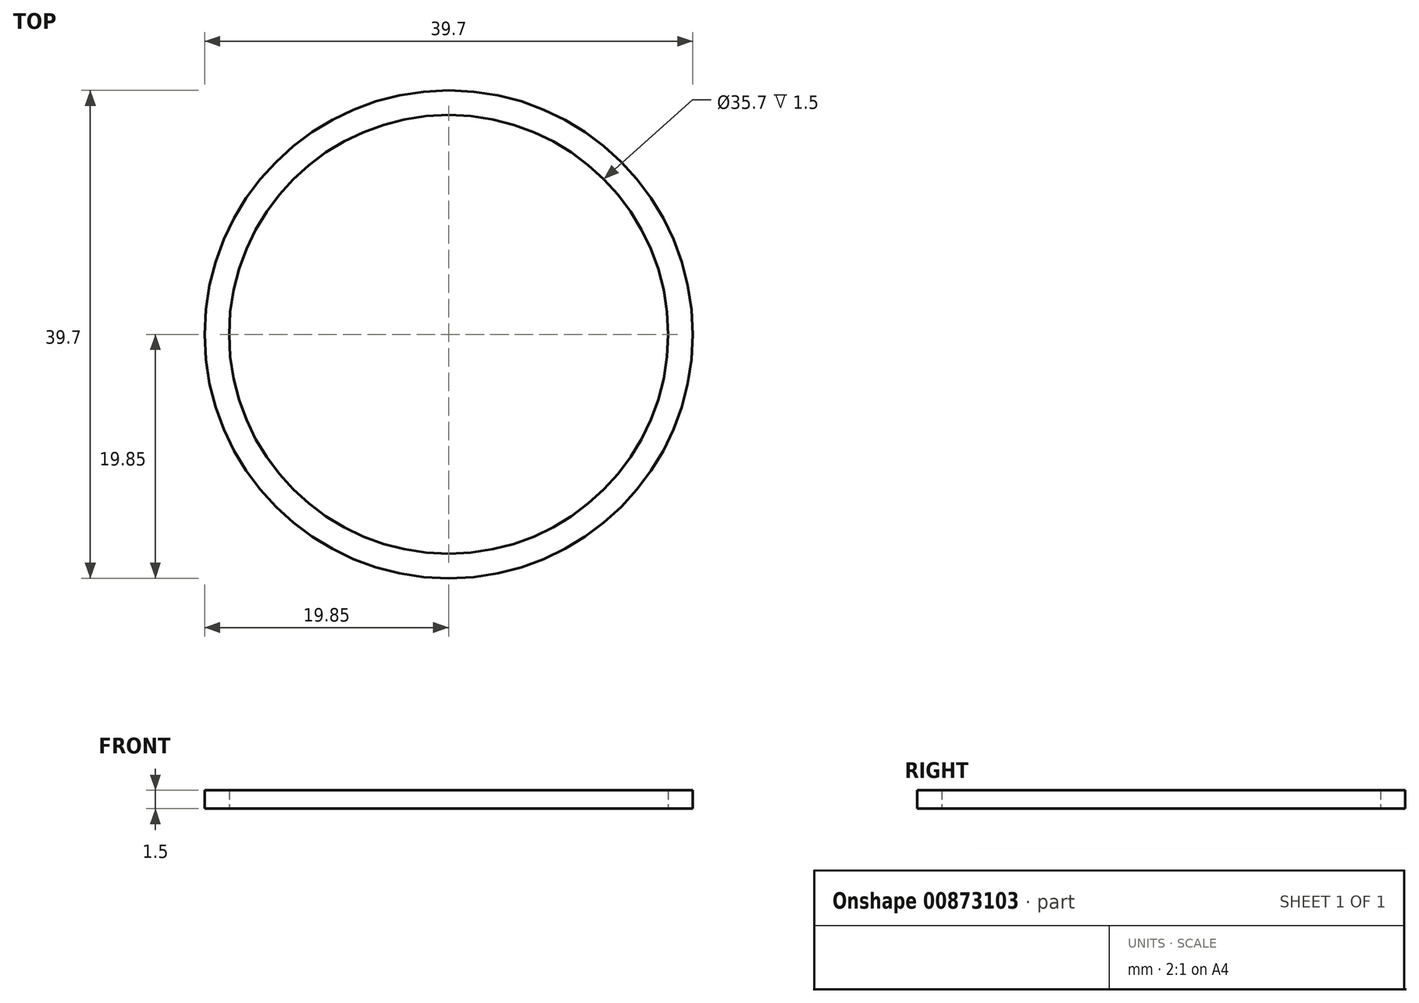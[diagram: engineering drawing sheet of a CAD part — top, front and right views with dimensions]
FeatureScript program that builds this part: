
annotation { "Feature Type Name" : "Feature", "Feature Type Description" : "" }
export const myFeature = defineFeature(function(context is Context, id is Id, definition is map)
    precondition{}
    {
        {
            var Q0;
            Q0=qCreatedBy(makeId("Top.planeOp"),FACE);
            var sketch = newSketch(context, id + "F0", { "sketchPlane" : qUnion([Q0])});
            skCircle(sketch, "E0", {"center": v(0, 0) * mm, "radius": 19.85 * mm});
            skCircle(sketch, "E1.0", {"center": v(0, 0) * mm, "radius": 17.85 * mm});
            skSolve(sketch);
        }
        {
            var Q0;
            Q0=makeQuery(id+"F0.imprint","IMPRINT",FACE,{"disambiguationData":[TD([[makeQuery(id+"F0.imprint","IMPRINT",EDGE,{"derivedFrom":sQuery(id+"F0.wireOp",EDGE,"E0")}),1.0]])]});
            extrude(context, id + "F1", {"entities" : qUnion([Q0]), "depth" : 1.5 * mm, "offsetDistance" : 25 * mm});
        }
    });
